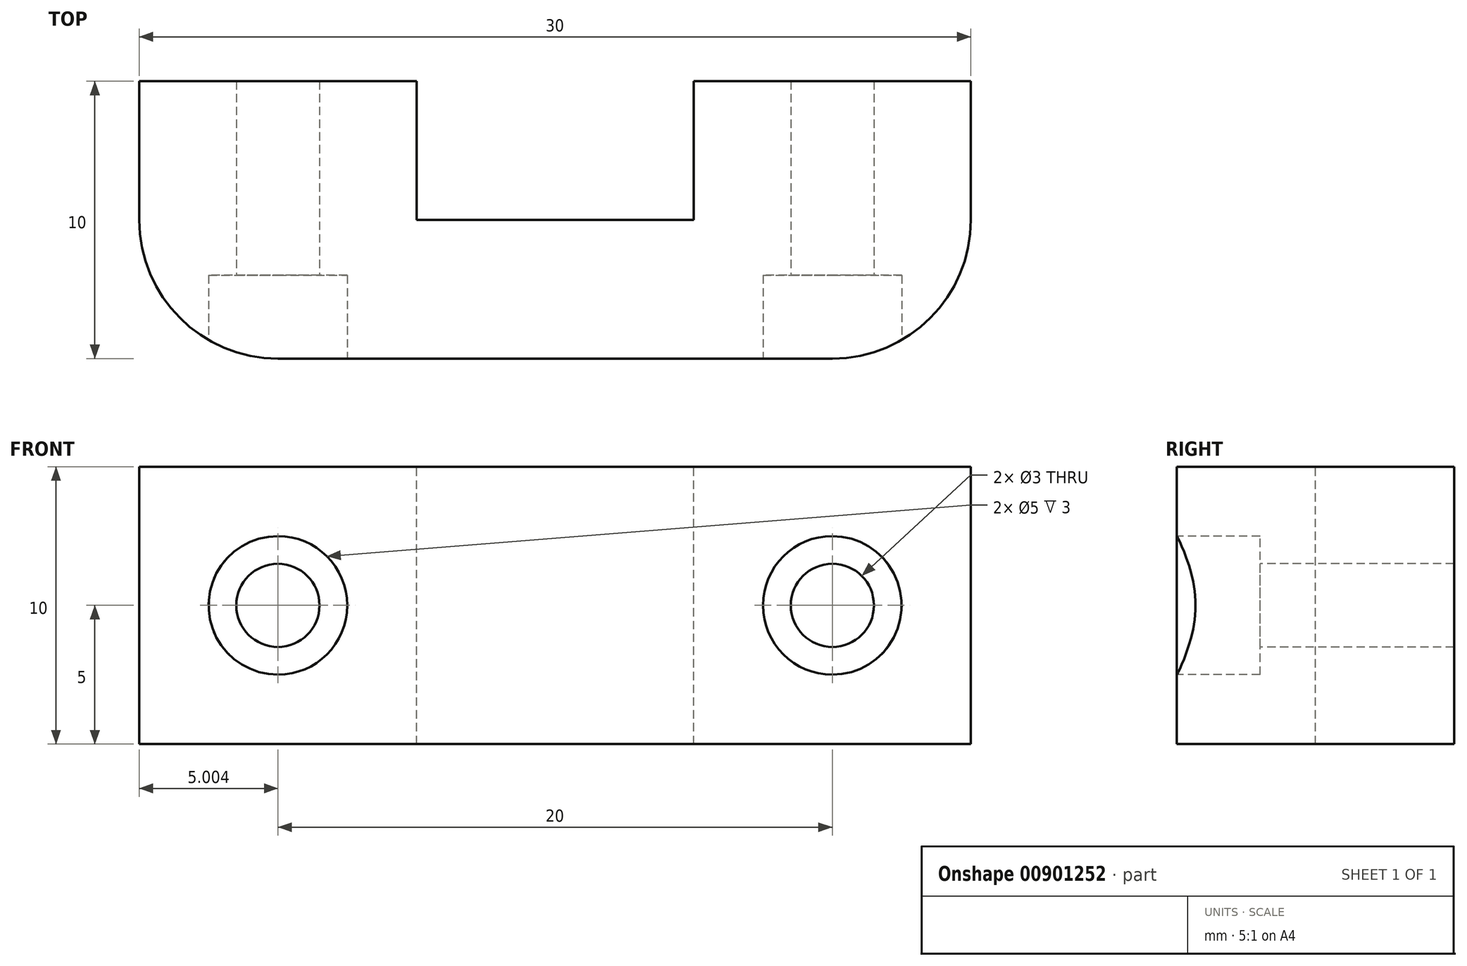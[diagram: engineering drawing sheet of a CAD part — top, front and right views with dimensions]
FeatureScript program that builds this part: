
annotation { "Feature Type Name" : "Feature", "Feature Type Description" : "" }
export const myFeature = defineFeature(function(context is Context, id is Id, definition is map)
    precondition{}
    {
        {
            var Q0;
            Q0=qCreatedBy(makeId("Front.planeOp"),FACE);
            var sketch = newSketch(context, id + "F0", { "sketchPlane" : qUnion([Q0])});
            skLineSegment(sketch, "E0", {"start": v(-29.23, 0) * mm, "end": v(0.77, 0) * mm});
            skLineSegment(sketch, "E1", {"start": v(0.77, 0) * mm, "end": v(0.77, 10) * mm});
            skLineSegment(sketch, "E2", {"start": v(0.77, 10) * mm, "end": v(-29.23, 10) * mm});
            skLineSegment(sketch, "E3", {"start": v(-29.23, 10) * mm, "end": v(-29.23, 0) * mm});
            skSolve(sketch);
        }
        {
            var Q0;
            Q0 = qSketchRegion(id + "F0", true);
            extrude(context, id + "F1", {"entities" : qUnion([Q0]), "depth" : 10 * mm, "offsetDistance" : 25 * mm});
        }
        {
            var Q0;
            Q0=makeQuery(id+"F1.opExtrude","SWEPT_FACE",FACE,{"disambiguationData":[OSD([sQuery(id+"F0.wireOp",EDGE,"E2")])]});
            var sketch = newSketch(context, id + "F2", { "sketchPlane" : qUnion([Q0])});
            skLineSegment(sketch, "E4", {"start": v(-14.23, 0) * mm, "end": v(-14.23, -5) * mm});
            skLineSegment(sketch, "E5", {"start": v(-14.23, -5) * mm, "end": v(-9.23, -5) * mm});
            skLineSegment(sketch, "E6", {"start": v(-9.23, -5) * mm, "end": v(-9.23, 0) * mm});
            skLineSegment(sketch, "E7", {"start": v(-9.23, 0) * mm, "end": v(-19.23, 0) * mm});
            skLineSegment(sketch, "E8", {"start": v(-19.23, 0) * mm, "end": v(-19.23, -5) * mm});
            skLineSegment(sketch, "E9", {"start": v(-19.23, -5) * mm, "end": v(-14.23, -5) * mm});
            skSolve(sketch);
        }
        {
            var Q0;
            Q0 = qSketchRegion(id + "F2", true);
            extrude(context, id + "F3", {"entities" : qUnion([Q0]), "operationType" : NewBodyOperationType.REMOVE, "oppositeDirection" : true, "depth" : 25 * mm, "offsetDistance" : 25 * mm});
        }
        {
            var Q0;
            Q0=makeQuery(id+"F1.opExtrude","CAP_EDGE",EDGE,{"disambiguationData":[OSD([sQuery(id+"F0.wireOp",EDGE,"E3")])],"isStart":false});
            var Q1;
            Q1=makeQuery(id+"F1.opExtrude","CAP_EDGE",EDGE,{"disambiguationData":[OSD([sQuery(id+"F0.wireOp",EDGE,"E1")])],"isStart":false});
            fillet(context, id + "F4", {"entities" : qUnion([Q0, Q1]), "radius" : 5 * mm, "tangentPropagation" : true, "allowEdgeOverflow" : false});
        }
        {
            var Q0;
            Q0=makeQuery(id+"F1.opExtrude","CAP_FACE",FACE,{"disambiguationData":[OSD([sQuery(id+"F0.wireOp",EDGE,"E0"),sQuery(id+"F0.wireOp",EDGE,"E1"),sQuery(id+"F0.wireOp",EDGE,"E2"),sQuery(id+"F0.wireOp",EDGE,"E3")])],"isStart":false});
            var sketch = newSketch(context, id + "F5", { "sketchPlane" : qUnion([Q0])});
            skCircle(sketch, "E10", {"center": v(-24.23, 5) * mm, "radius": 1.5 * mm});
            skCircle(sketch, "E11", {"center": v(-4.23, 5) * mm, "radius": 1.5 * mm});
            skSolve(sketch);
        }
        {
            var Q0;
            Q0 = qSketchRegion(id + "F5", true);
            extrude(context, id + "F6", {"entities" : qUnion([Q0]), "operationType" : NewBodyOperationType.REMOVE, "oppositeDirection" : true, "depth" : 25 * mm, "offsetDistance" : 25 * mm});
        }
        {
            var Q0;
            Q0=makeQuery(id+"F1.opExtrude","CAP_FACE",FACE,{"disambiguationData":[OSD([sQuery(id+"F0.wireOp",EDGE,"E0"),sQuery(id+"F0.wireOp",EDGE,"E1"),sQuery(id+"F0.wireOp",EDGE,"E2"),sQuery(id+"F0.wireOp",EDGE,"E3")])],"isStart":false});
            var sketch = newSketch(context, id + "F7", { "sketchPlane" : qUnion([Q0])});
            skCircle(sketch, "E12", {"center": v(-24.23, 5) * mm, "radius": 2.5 * mm});
            skCircle(sketch, "E13", {"center": v(-4.23, 5) * mm, "radius": 2.5 * mm});
            skSolve(sketch);
        }
        {
            var Q0;
            Q0 = qSketchRegion(id + "F7", true);
            extrude(context, id + "F8", {"entities" : qUnion([Q0]), "operationType" : NewBodyOperationType.REMOVE, "oppositeDirection" : true, "depth" : 3 * mm, "offsetDistance" : 25 * mm});
        }
    });
